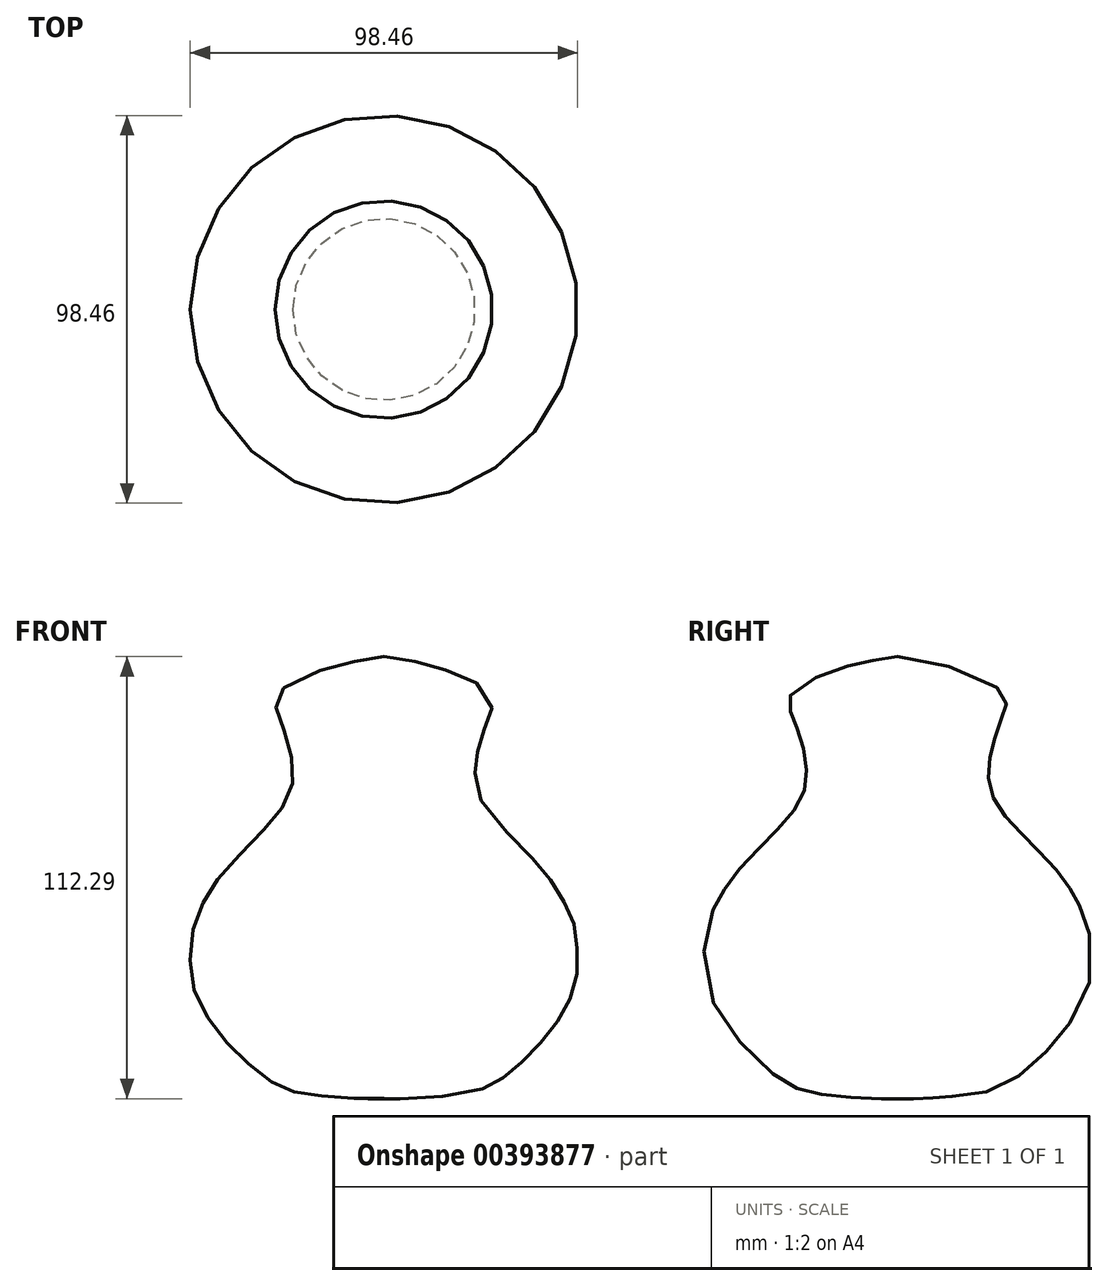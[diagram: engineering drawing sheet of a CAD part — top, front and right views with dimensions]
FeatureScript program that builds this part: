
annotation { "Feature Type Name" : "Feature", "Feature Type Description" : "" }
export const myFeature = defineFeature(function(context is Context, id is Id, definition is map)
    precondition{}
    {
        {
            var Q0;
            Q0=qCreatedBy(makeId("Front.planeOp"),FACE);
            var sketch = newSketch(context, id + "F0", { "sketchPlane" : qUnion([Q0])});
            skFitSpline(sketch, "E0", {"points": [v(0, 63.34) * mm, v(-7.11, 62.23) * mm, v(-16.9, 59.56) * mm, v(-26.9, 54) * mm, v(-27.56, 50.9) * mm, v(-26.67, 48.23) * mm, v(-24.23, 41.12) * mm, v(-23.34, 36.45) * mm, v(-23.34, 30.67) * mm, v(-25.56, 25.34) * mm, v(-29.56, 20.45) * mm, v(-36, 13.78) * mm, v(-42, 7.11) * mm, v(-45.34, 1.78) * mm, v(-48, -3.78) * mm, v(-49.12, -11.33) * mm, v(-48.9, -18.67) * mm, v(-46.45, -25.34) * mm, v(-42, -32.23) * mm, v(-36.67, -38) * mm, v(-31.78, -42.45) * mm, v(-26.23, -46) * mm, v(-22.22, -47.34) * mm, v(-15.56, -48.23) * mm, v(-7.11, -48.9) * mm, v(0, -48.9) * mm], "startDerivative": vector(-168.93, -23.32) * mm, "endDerivative": vector(169.2, 3.52) * mm});
            skLineSegment(sketch, "E1", {"start": v(0, 63.34) * mm, "end": v(0, -48.9) * mm});
            skSolve(sketch);
        }
        {
            var Q0;
            Q0=makeQuery(id+"F0.imprint","IMPRINT",FACE,{"disambiguationData":[TD([[makeQuery(id+"F0.imprint","IMPRINT",EDGE,{"derivedFrom":sQuery(id+"F0.wireOp",EDGE,"E0")}),1.0]])]});
            var Q1;
            Q1=sQuery(id+"F0.wireOp",EDGE,"E1");
            revolve(context, id + "F1", {"entities" : qUnion([Q0]), "axis" : qUnion([Q1]), "revolveType" : RevolveType.FULL});
        }
    });
